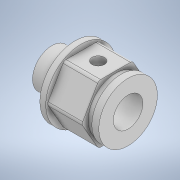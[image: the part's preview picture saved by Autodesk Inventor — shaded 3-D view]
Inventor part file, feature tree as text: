
AUTODESK INVENTOR PART (.ipt)
format: ipt  version: 2020 (Build 240168000, 168)  size: 379,392 bytes
history: native  units: mm
features: sketch x9, extrude x7, fillet x3
ambient origin geometry x8: Origin, YZ Plane, XZ Plane, XY Plane, X Axis, Y Axis, Z Axis, Center Point
bodies: Solid1 (feature_tree)
feature tree (19):
  extrude  "Extrusion1"  Depth=1.28mm TaperAngle=0.0deg
  extrude  "Extrusion2"  Depth=11.854mm
  extrude  "Extrusion3"  Depth=1.5mm TaperAngle=0.0deg
  extrude  "Extrusion4"  Depth=0.75mm
  fillet  "Fillet1"  Radius=2.705mm
  fillet  "Fillet2"  Radius=6.5mm
  sketch  "Sketch5"  dims[d15=6.4mm d16=11.75mm d17=0.0mm]
  extrude  "Extrusion5"  Depth=11.75mm TaperAngle=0.0deg
  sketch  "Sketch7"  dims[d21=2.0mm]
  sketch  "Sketch8"
  extrude  "Extrusion6"  Depth=5.0mm TaperAngle=0.0deg
  extrude  "Extrusion7"  [1 undecoded]
  fillet  "Fillet3"  [1 undecoded]
  sketch  "Sketch1"  dims[d0=15.197mm d1=1.28mm d2=0.0mm]
  sketch  "Sketch2"  dims[d3=7.5mm d4=0.0mm d5=11.854mm]
  sketch  "Sketch3"  dims[d6=1.22mm d7=0.0mm d8=1.5mm d9=0.0mm]
  sketch  "Sketch4"  dims[d10=0.75mm d11=0.75mm d12=2.705mm d13=6.5mm d14=0.0mm]
  sketch  "Sketch6"  dims[d18=8.4mm d19=5.0mm d20=0.0mm]
  sketch  "Sketch9"
note: 2 required parameter values undecoded (feature->parameter linkage not recoverable at this tier; creation-order binding heuristic only, values carry confidence <= 0.55)
